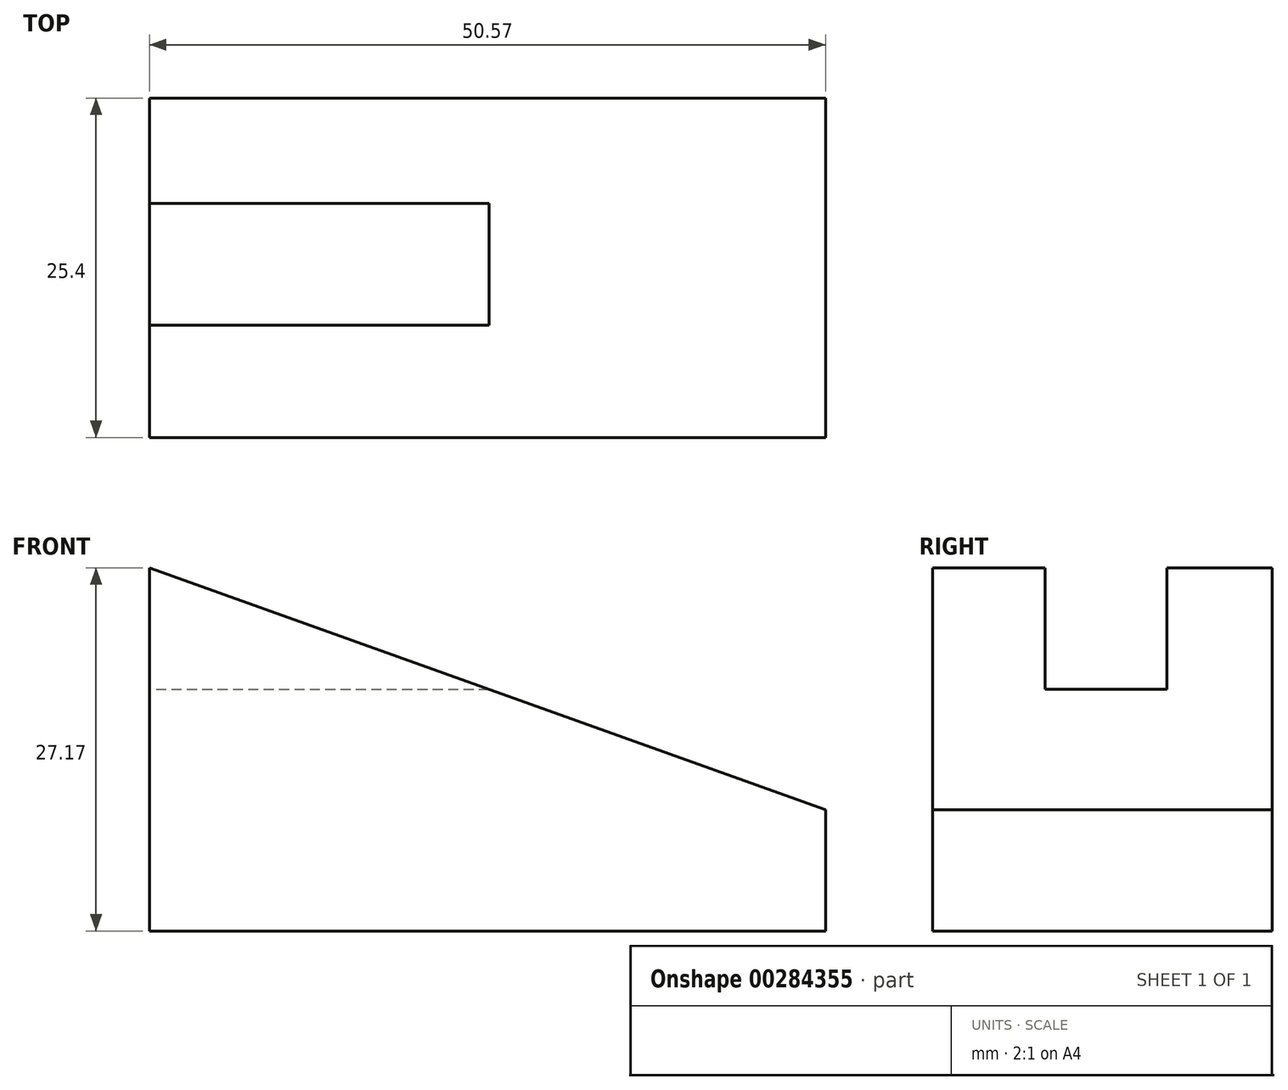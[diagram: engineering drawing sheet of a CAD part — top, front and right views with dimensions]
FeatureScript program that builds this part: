
annotation { "Feature Type Name" : "Feature", "Feature Type Description" : "" }
export const myFeature = defineFeature(function(context is Context, id is Id, definition is map)
    precondition{}
    {
        {
            var Q0;
            Q0=qCreatedBy(makeId("Front.planeOp"),FACE);
            var sketch = newSketch(context, id + "F0", { "sketchPlane" : qUnion([Q0])});
            skLineSegment(sketch, "E0", {"start": v(-50.57, 27.17) * mm, "end": v(-50.57, 0) * mm});
            skLineSegment(sketch, "E1", {"start": v(-50.57, 0) * mm, "end": v(0, 0) * mm});
            skLineSegment(sketch, "E2", {"start": v(0, 0) * mm, "end": v(0, 9.06) * mm});
            skLineSegment(sketch, "E3", {"start": v(0, 9.06) * mm, "end": v(-50.57, 9.06) * mm});
            skLineSegment(sketch, "E4", {"start": v(-50.57, 27.17) * mm, "end": v(0, 9.06) * mm});
            skLineSegment(sketch, "E5", {"start": v(-37.9, 22.63) * mm, "end": v(-50.57, 22.63) * mm});
            skLineSegment(sketch, "E6", {"start": v(-21.7, 16.83) * mm, "end": v(-21.7, 9.06) * mm});
            skSolve(sketch);
        }
        {
            var Q0;
            Q0 = qSketchRegion(id + "F0", true);
            var Q1;
            {var subQ3=sQuery(id+"F0.wireOp",EDGE,"E5");Q1=makeQuery(id+"F0.imprint","IMPRINT",FACE,{"disambiguationData":[TD([[makeQuery(id+"F0.imprint","IMPRINT",EDGE,{"derivedFrom":subQ3}),-1.0]])]});}
            var Q2;
            {var subQ3=sQuery(id+"F0.wireOp",EDGE,"E1");Q2=makeQuery(id+"F0.imprint","IMPRINT",FACE,{"disambiguationData":[TD([[makeQuery(id+"F0.imprint","IMPRINT",EDGE,{"derivedFrom":subQ3}),1.0]])]});}
            var Q3;
            {var subQ0=sQuery(id+"F0.wireOp",EDGE,"E5");Q3=makeQuery(id+"F0.imprint","IMPRINT",FACE,{"disambiguationData":[TD([[makeQuery(id+"F0.imprint","IMPRINT",EDGE,{"derivedFrom":subQ0}),1.0]])]});}
            extrude(context, id + "F1", {"entities" : qUnion([Q0, Q1, Q2, Q3]), "depth" : 25.4 * mm});
        }
        {
            var Q0;
            Q0=makeQuery(id+"F1.opExtrude","SWEPT_FACE",FACE,{"disambiguationData":[OSD([sQuery(id+"F0.wireOp",EDGE,"E0")])]});
            var sketch = newSketch(context, id + "F2", { "sketchPlane" : qUnion([Q0])});
            skLineSegment(sketch, "E7", {"start": v(7.88, 27.17) * mm, "end": v(7.88, 18.05) * mm});
            skLineSegment(sketch, "E8", {"start": v(16.98, 27.17) * mm, "end": v(16.98, 18.05) * mm});
            skLineSegment(sketch, "E9", {"start": v(16.98, 18.05) * mm, "end": v(7.88, 18.05) * mm});
            skLineSegment(sketch, "E10", {"start": v(7.88, 27.17) * mm, "end": v(16.98, 27.17) * mm});
            skSolve(sketch);
        }
        {
            var Q0;
            Q0=makeQuery(id+"F2.imprint","IMPRINT",FACE,{"disambiguationData":[TD([[makeQuery(id+"F2.imprint","IMPRINT",EDGE,{"derivedFrom":sQuery(id+"F2.wireOp",EDGE,"E7")}),1.0]])]});
            extrude(context, id + "F3", {"entities" : qUnion([Q0]), "operationType" : NewBodyOperationType.REMOVE, "oppositeDirection" : true, "depth" : 25.4 * mm});
        }
    });
